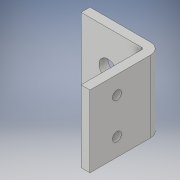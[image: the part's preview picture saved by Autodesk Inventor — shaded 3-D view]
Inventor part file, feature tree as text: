
AUTODESK INVENTOR PART (.ipt)
format: ipt  version: 2019 (Build 230136000, 136)  size: 130,560 bytes
history: native  units: in
note: dims shown in document units (in); Inventor stores cm internally (conversion verified against a paired STEP export)
features: extrude x3, sketch x3, fillet x1
ambient origin geometry x8: Origin, YZ Plane, XZ Plane, XY Plane, X Axis, Y Axis, Z Axis, Center Point
bodies: Solid1 (feature_tree)
feature tree (7):
  extrude  "Extrusion1"  Depth=4.0in
  extrude  "Extrusion2"  Depth=0.5in
  extrude  "Extrusion3"  Depth=0.625in
  fillet  "Fillet1"  Radius=4.0in
  sketch  "Sketch1"  dims[d0=4.0in d1=4.0in]
  sketch  "Sketch2"  dims[d2=0.5in d3=0.5in]
  sketch  "Sketch3"  dims[d4=0.625in d5=0.625in d6=4.0in d7=0.0in d8=0.5in d9=0.5in d10=1.0in d11=2.0in d12=1.5in d13=1.5in d14=4.0in d15=0.0in d16=1.0in d17=1.5in d18=2.0in d19=4.0in d20=0.0in d21=0.125in]
